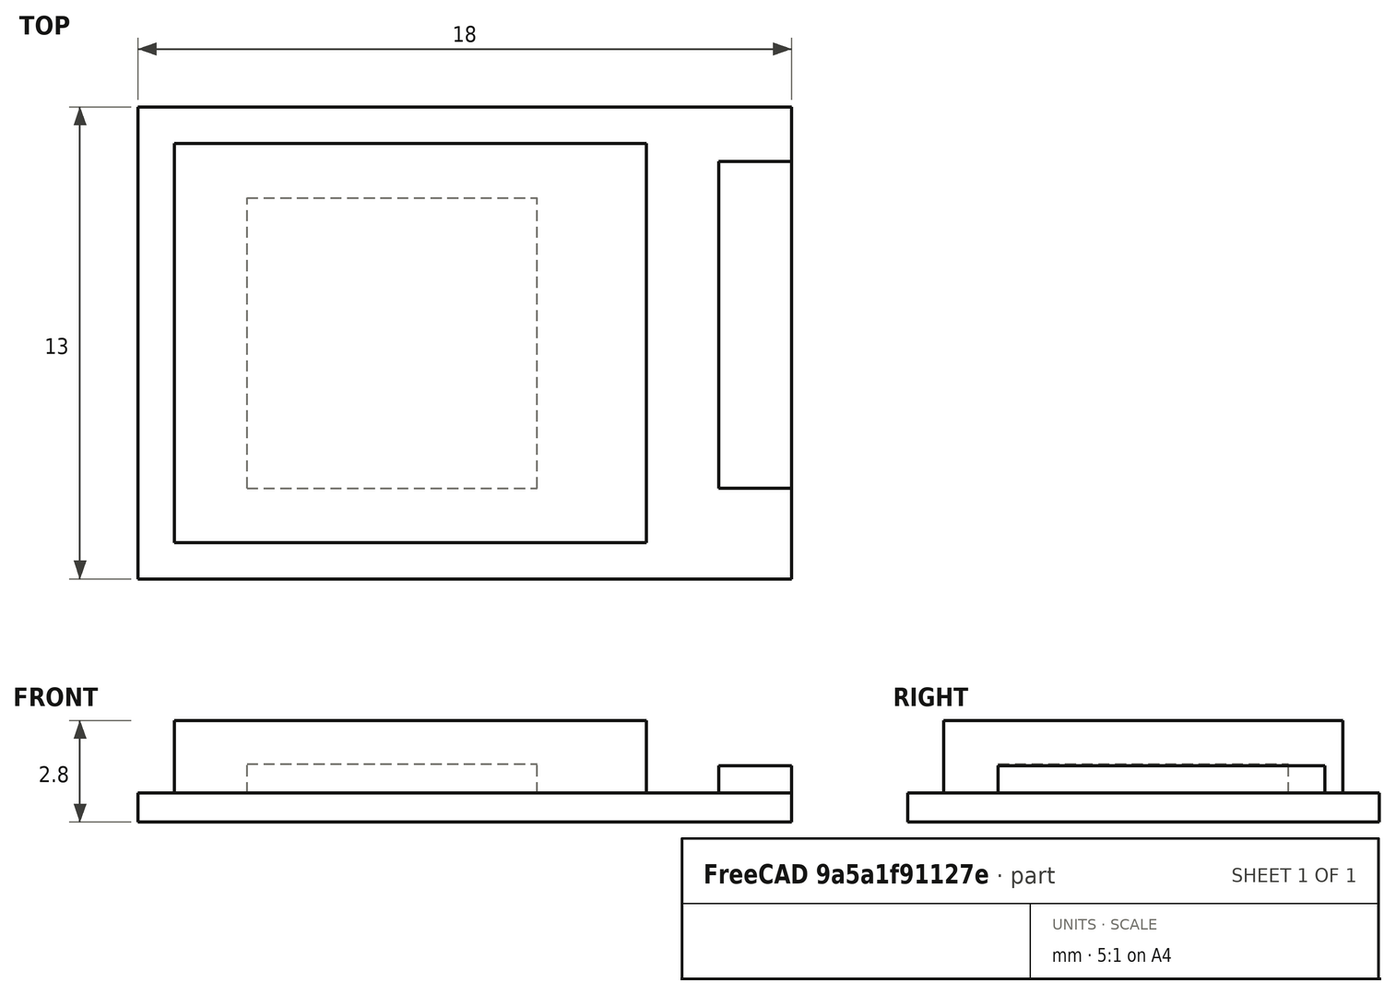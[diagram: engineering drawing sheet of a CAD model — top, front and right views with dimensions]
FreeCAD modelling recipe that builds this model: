
FCSTD DOCUMENT  (FreeCAD 0.17R13541 (Git))
Label: E73-2G4M08S1C
License: All rights reserved
LicenseURL: http://en.wikipedia.org/wiki/All_rights_reserved
objects: Part::Box×4, Part::Part2DObjectPython×1
note: 5 computed .brp shape members not serialized (recipe doc carries the construction recipe); baked Part::Feature solids carry a one-line shape summary decoded from their .brp

FEATURE [Part::Box] Box  label="PCB"
  AttacherType = Attacher::AttachEngine3D
  Height = 0.8
  Length = 18
  Placement = pos=(0,-6.5,0) rot=(0,0,1;0rad)
  Width = 13
FEATURE [Part::Box] Box001  label="Shield"
  AttacherType = Attacher::AttachEngine3D
  Height = 2
  Length = 13
  Placement = pos=(1,-5.5,0.8) rot=(0,0,1;0rad)
  Width = 11
FEATURE [Part::Box] Box002  label="Antenna"
  AttacherType = Attacher::AttachEngine3D
  Height = 0.75
  Length = 2
  Placement = pos=(16,-4,0.8) rot=(0,0,1;0rad)
  Width = 9
FEATURE [Part::Part2DObjectPython] ShapeString  # Draft 2D object (typed FeaturePython)
  FontFile = <path>
  Placement = pos=(2.12,3.49,2.81) rot=(0,0,1;0rad)
  Size = 1
  String = E73-2G4M08S1C
  Tracking = 0
FEATURE [Part::Box] Box003  label="MCU"
  AttacherType = Attacher::AttachEngine3D
  Height = 0.8
  Length = 8
  Placement = pos=(3,-4,0.8) rot=(0,0,1;0rad)
  Width = 8
note: 1 file-system path scrubbed to <path> (originals preserved in the JSON sidecar)
